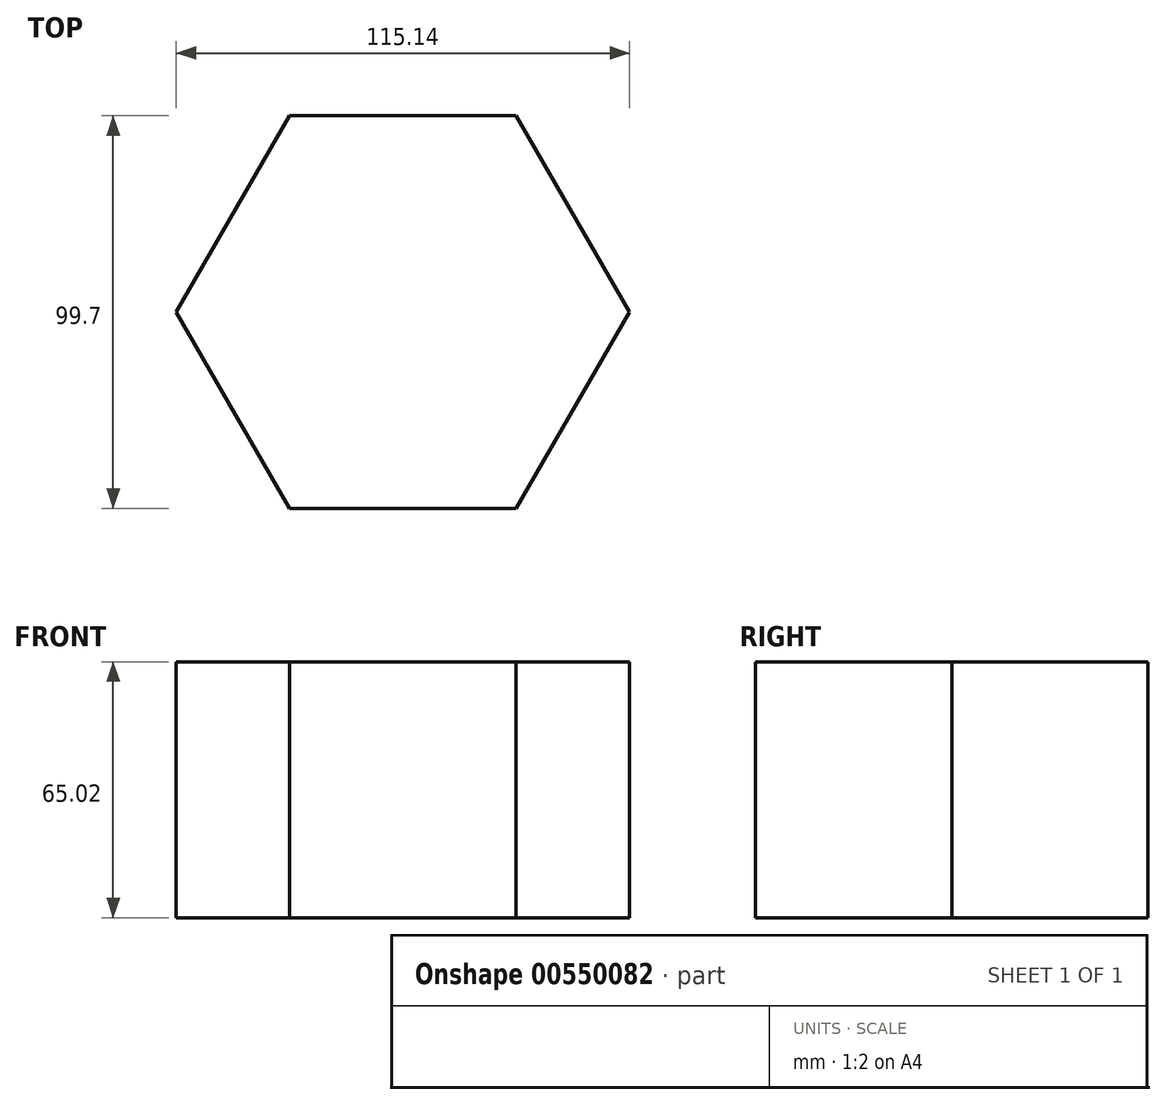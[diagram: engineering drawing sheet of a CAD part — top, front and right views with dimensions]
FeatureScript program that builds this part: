
annotation { "Feature Type Name" : "Feature", "Feature Type Description" : "" }
export const myFeature = defineFeature(function(context is Context, id is Id, definition is map)
    precondition{}
    {
        {
            var Q0;
            Q0=qCreatedBy(makeId("Top.planeOp"),FACE);
            var sketch = newSketch(context, id + "F0", { "sketchPlane" : qUnion([Q0])});
            skCircle(sketch, "E0.cCircle", {"center": v(0, 0) * mm, "radius": 49.85 * mm, "construction": true});
            skLineSegment(sketch, "E0.0", {"start": v(28.78, -49.85) * mm, "end": v(-28.78, -49.85) * mm});
            skLineSegment(sketch, "E0.1", {"start": v(-28.78, -49.85) * mm, "end": v(-57.57, 0) * mm});
            skLineSegment(sketch, "E0.2", {"start": v(-57.57, 0) * mm, "end": v(-28.78, 49.85) * mm});
            skLineSegment(sketch, "E0.3", {"start": v(-28.78, 49.85) * mm, "end": v(28.78, 49.85) * mm});
            skLineSegment(sketch, "E0.4", {"start": v(28.78, 49.85) * mm, "end": v(57.57, 0) * mm});
            skLineSegment(sketch, "E0.5", {"start": v(57.57, 0) * mm, "end": v(28.78, -49.85) * mm});
            skPoint(sketch, "E0.0.midPoint", {"position": v(0, -49.85) * mm});
            skSolve(sketch);
        }
        {
            var Q0;
            Q0=makeQuery(id+"F0.imprint","IMPRINT",FACE,{"disambiguationData":[TD([[makeQuery(id+"F0.imprint","IMPRINT",EDGE,{"derivedFrom":sQuery(id+"F0.wireOp",EDGE,"E0.0")}),-1.0]])]});
            extrude(context, id + "F1", {"entities" : qUnion([Q0]), "depth" : 65.02 * mm, "offsetDistance" : 25.4 * mm});
        }
    });
